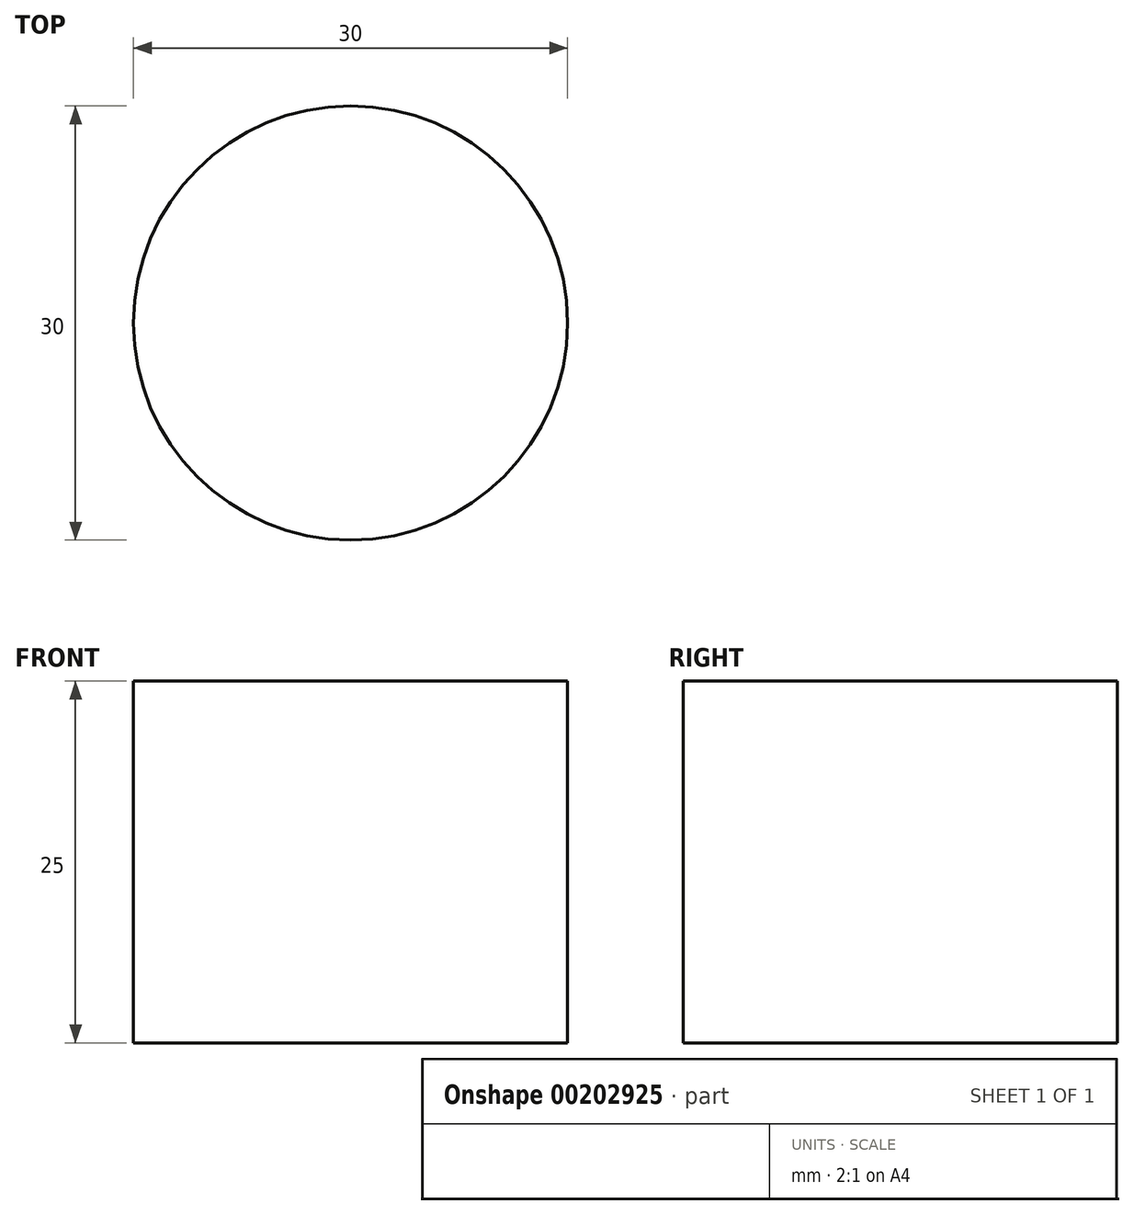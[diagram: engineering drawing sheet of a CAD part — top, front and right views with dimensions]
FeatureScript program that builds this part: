
annotation { "Feature Type Name" : "Feature", "Feature Type Description" : "" }
export const myFeature = defineFeature(function(context is Context, id is Id, definition is map)
    precondition{}
    {
        {
            var Q0;
            Q0=qCreatedBy(makeId("Top.planeOp"),FACE);
            var sketch = newSketch(context, id + "F0", { "sketchPlane" : qUnion([Q0])});
            skCircle(sketch, "E0", {"center": v(0, 0) * mm, "radius": 15 * mm});
            skSolve(sketch);
        }
        {
            var Q0;
            Q0 = qSketchRegion(id + "F0", true);
            extrude(context, id + "F1", {"entities" : qUnion([Q0]), "depth" : 25 * mm});
        }
    });
